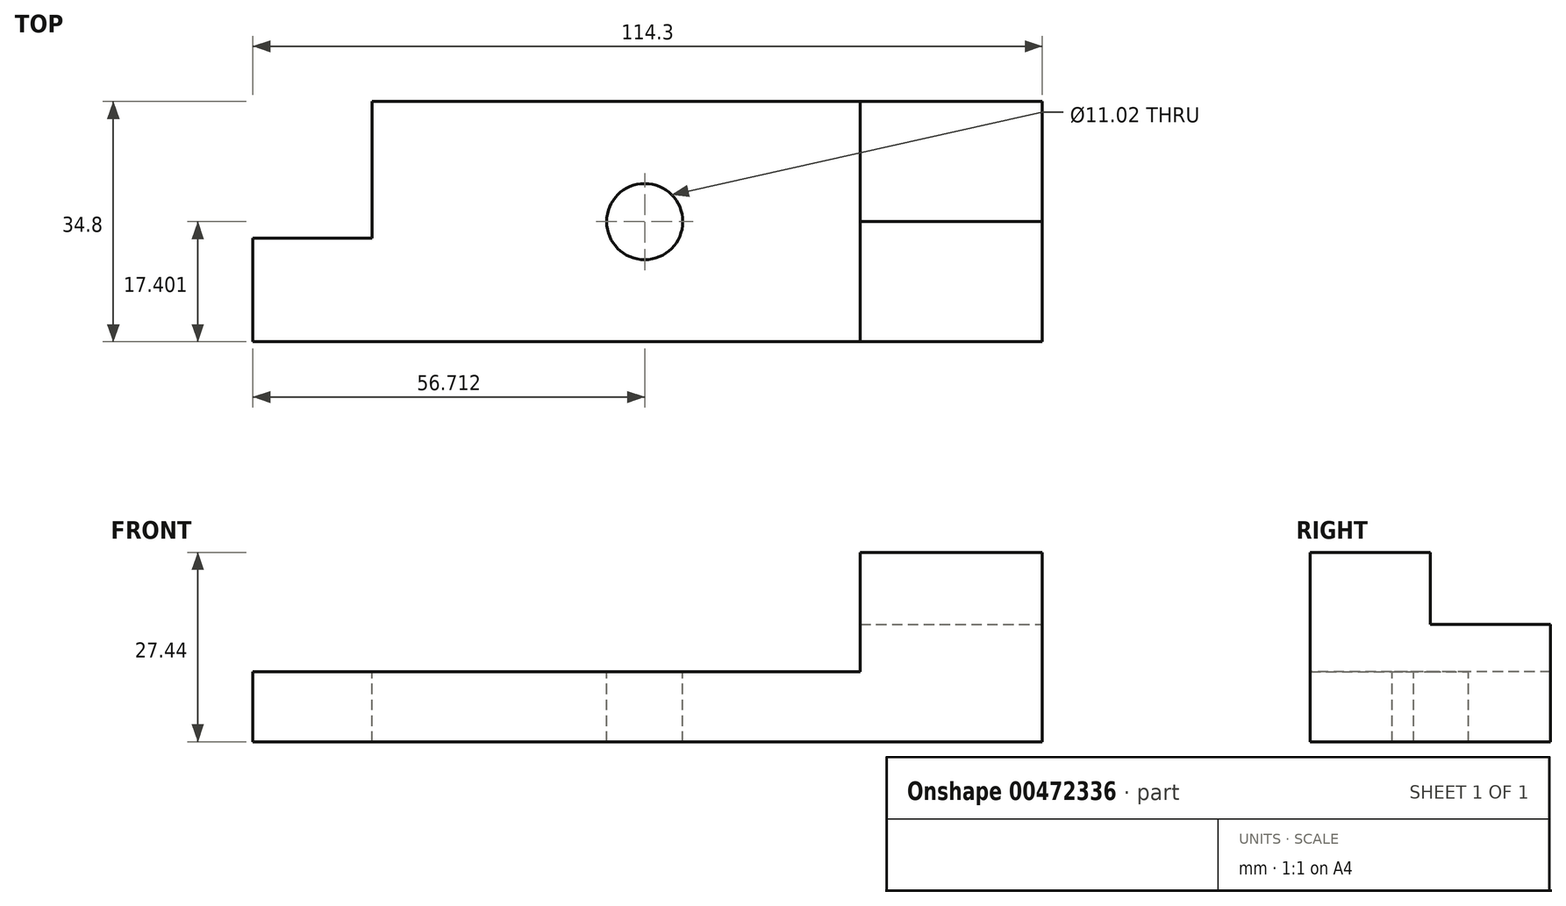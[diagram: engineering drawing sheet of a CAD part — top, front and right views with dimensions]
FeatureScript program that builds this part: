
annotation { "Feature Type Name" : "Feature", "Feature Type Description" : "" }
export const myFeature = defineFeature(function(context is Context, id is Id, definition is map)
    precondition{}
    {
        {
            var Q0;
            Q0=qCreatedBy(makeId("Front.planeOp"),FACE);
            var sketch = newSketch(context, id + "F0", { "sketchPlane" : qUnion([Q0])});
            skLineSegment(sketch, "E0", {"start": v(-51.08, 0) * mm, "end": v(63.22, 0) * mm});
            skLineSegment(sketch, "E1", {"start": v(63.22, 0) * mm, "end": v(-51.08, 0) * mm});
            skLineSegment(sketch, "E2", {"start": v(-51.08, 0) * mm, "end": v(-51.08, 10.17) * mm});
            skLineSegment(sketch, "E3", {"start": v(-51.08, 10.17) * mm, "end": v(63.22, 10.17) * mm});
            skLineSegment(sketch, "E4", {"start": v(63.22, 10.17) * mm, "end": v(63.22, 0) * mm});
            skSolve(sketch);
        }
        {
            var Q0;
            Q0 = qSketchRegion(id + "F0", true);
            extrude(context, id + "F1", {"entities" : qUnion([Q0]), "depth" : 34.8 * mm});
        }
        {
            var Q0;
            Q0=makeQuery(id+"F1.opExtrude","SWEPT_FACE",FACE,{"disambiguationData":[OSD([sQuery(id+"F0.wireOp",EDGE,"E3")])]});
            var sketch = newSketch(context, id + "F2", { "sketchPlane" : qUnion([Q0])});
            skLineSegment(sketch, "E5", {"start": v(-33.85, 0) * mm, "end": v(-33.85, -19.8) * mm});
            skLineSegment(sketch, "E6", {"start": v(-33.85, -19.8) * mm, "end": v(-51.08, -19.8) * mm});
            skLineSegment(sketch, "E7", {"start": v(-51.08, -19.8) * mm, "end": v(-51.08, 0) * mm});
            skSolve(sketch);
        }
        {
            var Q0;
            {var subQ0=sQuery(id+"F2.wireOp",EDGE,"E5");Q0=makeQuery(id+"F2.imprint","IMPRINT",FACE,{"disambiguationData":[TD([[makeQuery(id+"F2.imprint","IMPRINT",EDGE,{"derivedFrom":subQ0}),-1.0]])]});}
            extrude(context, id + "F3", {"entities" : qUnion([Q0]), "operationType" : NewBodyOperationType.REMOVE, "oppositeDirection" : true, "depth" : 25.4 * mm});
        }
        {
            var Q0;
            Q0=makeQuery(id+"F1.opExtrude","SWEPT_FACE",FACE,{"disambiguationData":[OSD([sQuery(id+"F0.wireOp",EDGE,"E3")])]});
            var sketch = newSketch(context, id + "F4", { "sketchPlane" : qUnion([Q0])});
            skLineSegment(sketch, "E8", {"start": v(63.22, 0) * mm, "end": v(36.84, 0) * mm});
            skLineSegment(sketch, "E9", {"start": v(36.84, 0) * mm, "end": v(36.84, -34.8) * mm});
            skLineSegment(sketch, "E10", {"start": v(36.84, -34.8) * mm, "end": v(63.22, -34.8) * mm});
            skLineSegment(sketch, "E11", {"start": v(63.22, -34.8) * mm, "end": v(63.22, 0) * mm});
            skSolve(sketch);
        }
        {
            var Q0;
            Q0 = qSketchRegion(id + "F4", true);
            extrude(context, id + "F5", {"entities" : qUnion([Q0]), "operationType" : NewBodyOperationType.ADD, "depth" : 17.27 * mm});
        }
        {
            var Q0;
            Q0=makeQuery(id+"F5.opExtrude","CAP_FACE",FACE,{"disambiguationData":[OSD([sQuery(id+"F4.wireOp",EDGE,"E8"),sQuery(id+"F4.wireOp",EDGE,"E9"),sQuery(id+"F4.wireOp",EDGE,"E10"),sQuery(id+"F4.wireOp",EDGE,"E11")])],"isStart":false});
            var sketch = newSketch(context, id + "F6", { "sketchPlane" : qUnion([Q0])});
            skLineSegment(sketch, "E12", {"start": v(63.22, -17.4) * mm, "end": v(36.84, -17.4) * mm});
            skLineSegment(sketch, "E13", {"start": v(36.84, -17.4) * mm, "end": v(36.84, 0) * mm});
            skLineSegment(sketch, "E14", {"start": v(36.84, 0) * mm, "end": v(63.22, 0) * mm});
            skLineSegment(sketch, "E15", {"start": v(63.22, 0) * mm, "end": v(63.22, -17.4) * mm});
            skSolve(sketch);
        }
        {
            var Q0;
            Q0 = qSketchRegion(id + "F6", true);
            extrude(context, id + "F7", {"entities" : qUnion([Q0]), "operationType" : NewBodyOperationType.REMOVE, "oppositeDirection" : true, "depth" : 10.4 * mm});
        }
        {
            var Q0;
            Q0=makeQuery(id+"F1.opExtrude","SWEPT_FACE",FACE,{"disambiguationData":[OSD([sQuery(id+"F0.wireOp",EDGE,"E3")])]});
            var sketch = newSketch(context, id + "F8", { "sketchPlane" : qUnion([Q0])});
            skCircle(sketch, "E16", {"center": v(5.63, -17.4) * mm, "radius": 5.5 * mm});
            skPoint(sketch, "E16.centerSnap0", {"position": v(36.84, -17.4) * mm});
            skSolve(sketch);
        }
        {
            var Q0;
            Q0 = qSketchRegion(id + "F8", true);
            extrude(context, id + "F9", {"entities" : qUnion([Q0]), "operationType" : NewBodyOperationType.REMOVE, "oppositeDirection" : true, "depth" : 35.56 * mm});
        }
    });
